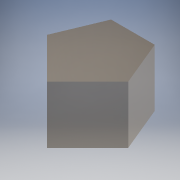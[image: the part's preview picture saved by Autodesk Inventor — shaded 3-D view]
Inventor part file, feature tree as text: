
AUTODESK INVENTOR PART (.ipt)
format: ipt  version: 2017 (Build 210142000, 142)  size: 98,816 bytes
history: native  units: mm
features: extrude x1, sketch x1
ambient origin geometry x8: Origin, YZ Plane, XZ Plane, XY Plane, X Axis, Y Axis, Z Axis, Center Point
bodies: Solid1 (feature_tree)
feature tree (2):
  extrude  "Extrusion1"  Depth=15.0mm
  sketch  "Sketch1"  dims[d0=90.0deg d1=112.5deg d2=112.5deg d3=112.5deg d4=15.0mm d5=12.805mm d6=15.0mm d7=0.0mm]
